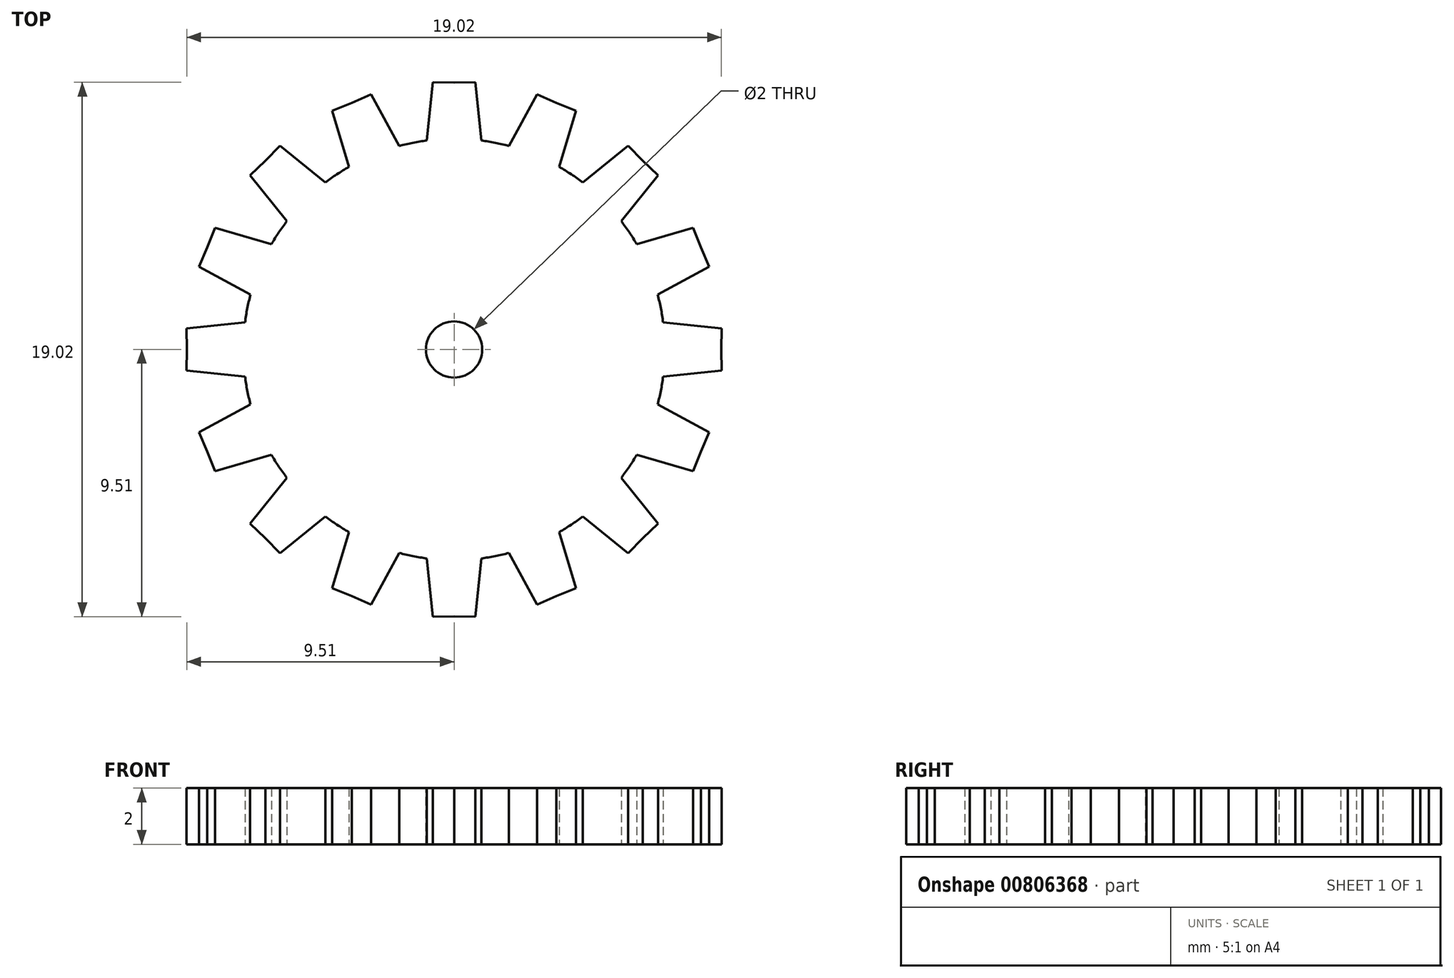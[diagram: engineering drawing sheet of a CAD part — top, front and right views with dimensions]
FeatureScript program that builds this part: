
annotation { "Feature Type Name" : "Feature", "Feature Type Description" : "" }
export const myFeature = defineFeature(function(context is Context, id is Id, definition is map)
    precondition{}
    {
        {
            var Q0;
            Q0=qCreatedBy(makeId("Top.planeOp"),FACE);
            var sketch = newSketch(context, id + "F0", { "sketchPlane" : qUnion([Q0])});
            skCircle(sketch, "E0", {"center": v(0, 0) * mm, "radius": 7.5 * mm});
            skLineSegment(sketch, "E1", {"start": v(0, 0) * mm, "end": v(0, 7.5) * mm, "construction": true});
            skPoint(sketch, "E2.end.orphan", {"position": v(0, 9.5) * mm});
            skPoint(sketch, "E3.end.orphan", {"position": v(-1.37, 9.64) * mm});
            skPoint(sketch, "E3.start.orphan", {"position": v(-0.97, 7.44) * mm});
            skPoint(sketch, "E4.MirrorCS.start.orphan", {"position": v(1.37, 9.64) * mm});
            skPoint(sketch, "E5.MirrorCS.start.orphan", {"position": v(0.97, 7.44) * mm});
            skLineSegment(sketch, "E6", {"start": v(-0.97, 7.44) * mm, "end": v(-0.75, 9.51) * mm});
            skLineSegment(sketch, "E7", {"start": v(-0.75, 9.51) * mm, "end": v(0, 9.5) * mm});
            skLineSegment(sketch, "E8.MirrorCS", {"start": v(0.97, 7.44) * mm, "end": v(0.75, 9.51) * mm});
            skLineSegment(sketch, "E9.MirrorCS", {"start": v(0.75, 9.51) * mm, "end": v(0, 9.5) * mm});
            skLineSegment(sketch, "E10.1.0", {"start": v(-3.74, 6.5) * mm, "end": v(-4.33, 8.5) * mm});
            skLineSegment(sketch, "E10.1.1", {"start": v(-4.33, 8.5) * mm, "end": v(-3.64, 8.78) * mm});
            skLineSegment(sketch, "E10.1.2", {"start": v(-2.95, 9.08) * mm, "end": v(-3.64, 8.78) * mm});
            skLineSegment(sketch, "E10.1.3", {"start": v(-1.95, 7.24) * mm, "end": v(-2.95, 9.08) * mm});
            skLineSegment(sketch, "E10.2.0", {"start": v(-5.94, 4.57) * mm, "end": v(-7.26, 6.2) * mm});
            skLineSegment(sketch, "E10.2.1", {"start": v(-7.26, 6.2) * mm, "end": v(-6.72, 6.72) * mm});
            skLineSegment(sketch, "E10.2.2", {"start": v(-6.2, 7.26) * mm, "end": v(-6.72, 6.72) * mm});
            skLineSegment(sketch, "E10.2.3", {"start": v(-4.57, 5.94) * mm, "end": v(-6.2, 7.26) * mm});
            skLineSegment(sketch, "E10.3.0", {"start": v(-7.24, 1.95) * mm, "end": v(-9.08, 2.95) * mm});
            skLineSegment(sketch, "E10.3.1", {"start": v(-9.08, 2.95) * mm, "end": v(-8.78, 3.64) * mm});
            skLineSegment(sketch, "E10.3.2", {"start": v(-8.5, 4.33) * mm, "end": v(-8.78, 3.64) * mm});
            skLineSegment(sketch, "E10.3.3", {"start": v(-6.5, 3.74) * mm, "end": v(-8.5, 4.33) * mm});
            skLineSegment(sketch, "E10.4.0", {"start": v(-7.44, -0.97) * mm, "end": v(-9.51, -0.75) * mm});
            skLineSegment(sketch, "E10.4.1", {"start": v(-9.51, -0.75) * mm, "end": v(-9.5, 0) * mm});
            skLineSegment(sketch, "E10.4.2", {"start": v(-9.51, 0.75) * mm, "end": v(-9.5, 0) * mm});
            skLineSegment(sketch, "E10.4.3", {"start": v(-7.44, 0.97) * mm, "end": v(-9.51, 0.75) * mm});
            skLineSegment(sketch, "E10.5.0", {"start": v(-6.5, -3.74) * mm, "end": v(-8.5, -4.33) * mm});
            skLineSegment(sketch, "E10.5.1", {"start": v(-8.5, -4.33) * mm, "end": v(-8.78, -3.64) * mm});
            skLineSegment(sketch, "E10.5.2", {"start": v(-9.08, -2.95) * mm, "end": v(-8.78, -3.64) * mm});
            skLineSegment(sketch, "E10.5.3", {"start": v(-7.24, -1.95) * mm, "end": v(-9.08, -2.95) * mm});
            skLineSegment(sketch, "E10.6.0", {"start": v(-4.57, -5.94) * mm, "end": v(-6.2, -7.26) * mm});
            skLineSegment(sketch, "E10.6.1", {"start": v(-6.2, -7.26) * mm, "end": v(-6.72, -6.72) * mm});
            skLineSegment(sketch, "E10.6.2", {"start": v(-7.26, -6.2) * mm, "end": v(-6.72, -6.72) * mm});
            skLineSegment(sketch, "E10.6.3", {"start": v(-5.94, -4.57) * mm, "end": v(-7.26, -6.2) * mm});
            skLineSegment(sketch, "E10.7.0", {"start": v(-1.95, -7.24) * mm, "end": v(-2.95, -9.08) * mm});
            skLineSegment(sketch, "E10.7.1", {"start": v(-2.95, -9.08) * mm, "end": v(-3.64, -8.78) * mm});
            skLineSegment(sketch, "E10.7.2", {"start": v(-4.33, -8.5) * mm, "end": v(-3.64, -8.78) * mm});
            skLineSegment(sketch, "E10.7.3", {"start": v(-3.74, -6.5) * mm, "end": v(-4.33, -8.5) * mm});
            skLineSegment(sketch, "E10.8.0", {"start": v(0.97, -7.44) * mm, "end": v(0.75, -9.51) * mm});
            skLineSegment(sketch, "E10.8.1", {"start": v(0.75, -9.51) * mm, "end": v(0, -9.5) * mm});
            skLineSegment(sketch, "E10.8.2", {"start": v(-0.75, -9.51) * mm, "end": v(0, -9.5) * mm});
            skLineSegment(sketch, "E10.8.3", {"start": v(-0.97, -7.44) * mm, "end": v(-0.75, -9.51) * mm});
            skLineSegment(sketch, "E10.9.0", {"start": v(3.74, -6.5) * mm, "end": v(4.33, -8.5) * mm});
            skLineSegment(sketch, "E10.9.1", {"start": v(4.33, -8.5) * mm, "end": v(3.64, -8.78) * mm});
            skLineSegment(sketch, "E10.9.2", {"start": v(2.95, -9.08) * mm, "end": v(3.64, -8.78) * mm});
            skLineSegment(sketch, "E10.9.3", {"start": v(1.95, -7.24) * mm, "end": v(2.95, -9.08) * mm});
            skLineSegment(sketch, "E10.10.0", {"start": v(5.94, -4.57) * mm, "end": v(7.26, -6.2) * mm});
            skLineSegment(sketch, "E10.10.1", {"start": v(7.26, -6.2) * mm, "end": v(6.72, -6.72) * mm});
            skLineSegment(sketch, "E10.10.2", {"start": v(6.2, -7.26) * mm, "end": v(6.72, -6.72) * mm});
            skLineSegment(sketch, "E10.10.3", {"start": v(4.57, -5.94) * mm, "end": v(6.2, -7.26) * mm});
            skLineSegment(sketch, "E10.11.0", {"start": v(7.24, -1.95) * mm, "end": v(9.08, -2.95) * mm});
            skLineSegment(sketch, "E10.11.1", {"start": v(9.08, -2.95) * mm, "end": v(8.78, -3.64) * mm});
            skLineSegment(sketch, "E10.11.2", {"start": v(8.5, -4.33) * mm, "end": v(8.78, -3.64) * mm});
            skLineSegment(sketch, "E10.11.3", {"start": v(6.5, -3.74) * mm, "end": v(8.5, -4.33) * mm});
            skLineSegment(sketch, "E10.12.0", {"start": v(7.44, 0.97) * mm, "end": v(9.51, 0.75) * mm});
            skLineSegment(sketch, "E10.12.1", {"start": v(9.51, 0.75) * mm, "end": v(9.5, 0) * mm});
            skLineSegment(sketch, "E10.12.2", {"start": v(9.51, -0.75) * mm, "end": v(9.5, 0) * mm});
            skLineSegment(sketch, "E10.12.3", {"start": v(7.44, -0.97) * mm, "end": v(9.51, -0.75) * mm});
            skLineSegment(sketch, "E10.13.0", {"start": v(6.5, 3.74) * mm, "end": v(8.5, 4.33) * mm});
            skLineSegment(sketch, "E10.13.1", {"start": v(8.5, 4.33) * mm, "end": v(8.78, 3.64) * mm});
            skLineSegment(sketch, "E10.13.2", {"start": v(9.08, 2.95) * mm, "end": v(8.78, 3.64) * mm});
            skLineSegment(sketch, "E10.13.3", {"start": v(7.24, 1.95) * mm, "end": v(9.08, 2.95) * mm});
            skLineSegment(sketch, "E10.14.0", {"start": v(4.57, 5.94) * mm, "end": v(6.2, 7.26) * mm});
            skLineSegment(sketch, "E10.14.1", {"start": v(6.2, 7.26) * mm, "end": v(6.72, 6.72) * mm});
            skLineSegment(sketch, "E10.14.2", {"start": v(7.26, 6.2) * mm, "end": v(6.72, 6.72) * mm});
            skLineSegment(sketch, "E10.14.3", {"start": v(5.94, 4.57) * mm, "end": v(7.26, 6.2) * mm});
            skLineSegment(sketch, "E10.15.0", {"start": v(1.95, 7.24) * mm, "end": v(2.95, 9.08) * mm});
            skLineSegment(sketch, "E10.15.1", {"start": v(2.95, 9.08) * mm, "end": v(3.64, 8.78) * mm});
            skLineSegment(sketch, "E10.15.2", {"start": v(4.33, 8.5) * mm, "end": v(3.64, 8.78) * mm});
            skLineSegment(sketch, "E10.15.3", {"start": v(3.74, 6.5) * mm, "end": v(4.33, 8.5) * mm});
            skSolve(sketch);
        }
        {
            var Q0;
            Q0 = qSketchRegion(id + "F0", true);
            extrude(context, id + "F1", {"entities" : qUnion([Q0]), "depth" : 2 * mm, "offsetDistance" : 25 * mm});
        }
        {
            var Q0;
            Q0=makeQuery(id+"F1.opExtrude","CAP_FACE",FACE,{"disambiguationData":[OSD([sQuery(id+"F0.wireOp",EDGE,"E0"),sQuery(id+"F0.wireOp",EDGE,"E6"),sQuery(id+"F0.wireOp",EDGE,"E7"),sQuery(id+"F0.wireOp",EDGE,"E8.MirrorCS"),sQuery(id+"F0.wireOp",EDGE,"E9.MirrorCS"),sQuery(id+"F0.wireOp",EDGE,"E10.1.0"),sQuery(id+"F0.wireOp",EDGE,"E10.1.1"),sQuery(id+"F0.wireOp",EDGE,"E10.1.2"),sQuery(id+"F0.wireOp",EDGE,"E10.1.3"),sQuery(id+"F0.wireOp",EDGE,"E10.2.0"),sQuery(id+"F0.wireOp",EDGE,"E10.2.1"),sQuery(id+"F0.wireOp",EDGE,"E10.2.2"),sQuery(id+"F0.wireOp",EDGE,"E10.2.3"),sQuery(id+"F0.wireOp",EDGE,"E10.3.0"),sQuery(id+"F0.wireOp",EDGE,"E10.3.1"),sQuery(id+"F0.wireOp",EDGE,"E10.3.2"),sQuery(id+"F0.wireOp",EDGE,"E10.3.3"),sQuery(id+"F0.wireOp",EDGE,"E10.4.0"),sQuery(id+"F0.wireOp",EDGE,"E10.4.1"),sQuery(id+"F0.wireOp",EDGE,"E10.4.2"),sQuery(id+"F0.wireOp",EDGE,"E10.4.3"),sQuery(id+"F0.wireOp",EDGE,"E10.5.0"),sQuery(id+"F0.wireOp",EDGE,"E10.5.1"),sQuery(id+"F0.wireOp",EDGE,"E10.5.2"),sQuery(id+"F0.wireOp",EDGE,"E10.5.3"),sQuery(id+"F0.wireOp",EDGE,"E10.6.0"),sQuery(id+"F0.wireOp",EDGE,"E10.6.1"),sQuery(id+"F0.wireOp",EDGE,"E10.6.2"),sQuery(id+"F0.wireOp",EDGE,"E10.6.3"),sQuery(id+"F0.wireOp",EDGE,"E10.7.0"),sQuery(id+"F0.wireOp",EDGE,"E10.7.1"),sQuery(id+"F0.wireOp",EDGE,"E10.7.2"),sQuery(id+"F0.wireOp",EDGE,"E10.7.3"),sQuery(id+"F0.wireOp",EDGE,"E10.8.0"),sQuery(id+"F0.wireOp",EDGE,"E10.8.1"),sQuery(id+"F0.wireOp",EDGE,"E10.8.2"),sQuery(id+"F0.wireOp",EDGE,"E10.8.3"),sQuery(id+"F0.wireOp",EDGE,"E10.9.0"),sQuery(id+"F0.wireOp",EDGE,"E10.9.1"),sQuery(id+"F0.wireOp",EDGE,"E10.9.2"),sQuery(id+"F0.wireOp",EDGE,"E10.9.3"),sQuery(id+"F0.wireOp",EDGE,"E10.10.0"),sQuery(id+"F0.wireOp",EDGE,"E10.10.1"),sQuery(id+"F0.wireOp",EDGE,"E10.10.2"),sQuery(id+"F0.wireOp",EDGE,"E10.10.3"),sQuery(id+"F0.wireOp",EDGE,"E10.11.0"),sQuery(id+"F0.wireOp",EDGE,"E10.11.1"),sQuery(id+"F0.wireOp",EDGE,"E10.11.2"),sQuery(id+"F0.wireOp",EDGE,"E10.11.3"),sQuery(id+"F0.wireOp",EDGE,"E10.12.0"),sQuery(id+"F0.wireOp",EDGE,"E10.12.1"),sQuery(id+"F0.wireOp",EDGE,"E10.12.2"),sQuery(id+"F0.wireOp",EDGE,"E10.12.3"),sQuery(id+"F0.wireOp",EDGE,"E10.13.0"),sQuery(id+"F0.wireOp",EDGE,"E10.13.1"),sQuery(id+"F0.wireOp",EDGE,"E10.13.2"),sQuery(id+"F0.wireOp",EDGE,"E10.13.3"),sQuery(id+"F0.wireOp",EDGE,"E10.14.0"),sQuery(id+"F0.wireOp",EDGE,"E10.14.1"),sQuery(id+"F0.wireOp",EDGE,"E10.14.2"),sQuery(id+"F0.wireOp",EDGE,"E10.14.3"),sQuery(id+"F0.wireOp",EDGE,"E10.15.0"),sQuery(id+"F0.wireOp",EDGE,"E10.15.1"),sQuery(id+"F0.wireOp",EDGE,"E10.15.2"),sQuery(id+"F0.wireOp",EDGE,"E10.15.3")])],"isStart":false});
            var sketch = newSketch(context, id + "F2", { "sketchPlane" : qUnion([Q0])});
            skCircle(sketch, "E11", {"center": v(0, 0) * mm, "radius": 1 * mm});
            skSolve(sketch);
        }
        {
            var Q0;
            Q0 = qSketchRegion(id + "F2", true);
            extrude(context, id + "F3", {"entities" : qUnion([Q0]), "operationType" : NewBodyOperationType.REMOVE, "endBound" : BoundingType.THROUGH_ALL, "oppositeDirection" : true, "depth" : 25 * mm, "offsetDistance" : 25 * mm});
        }
    });
